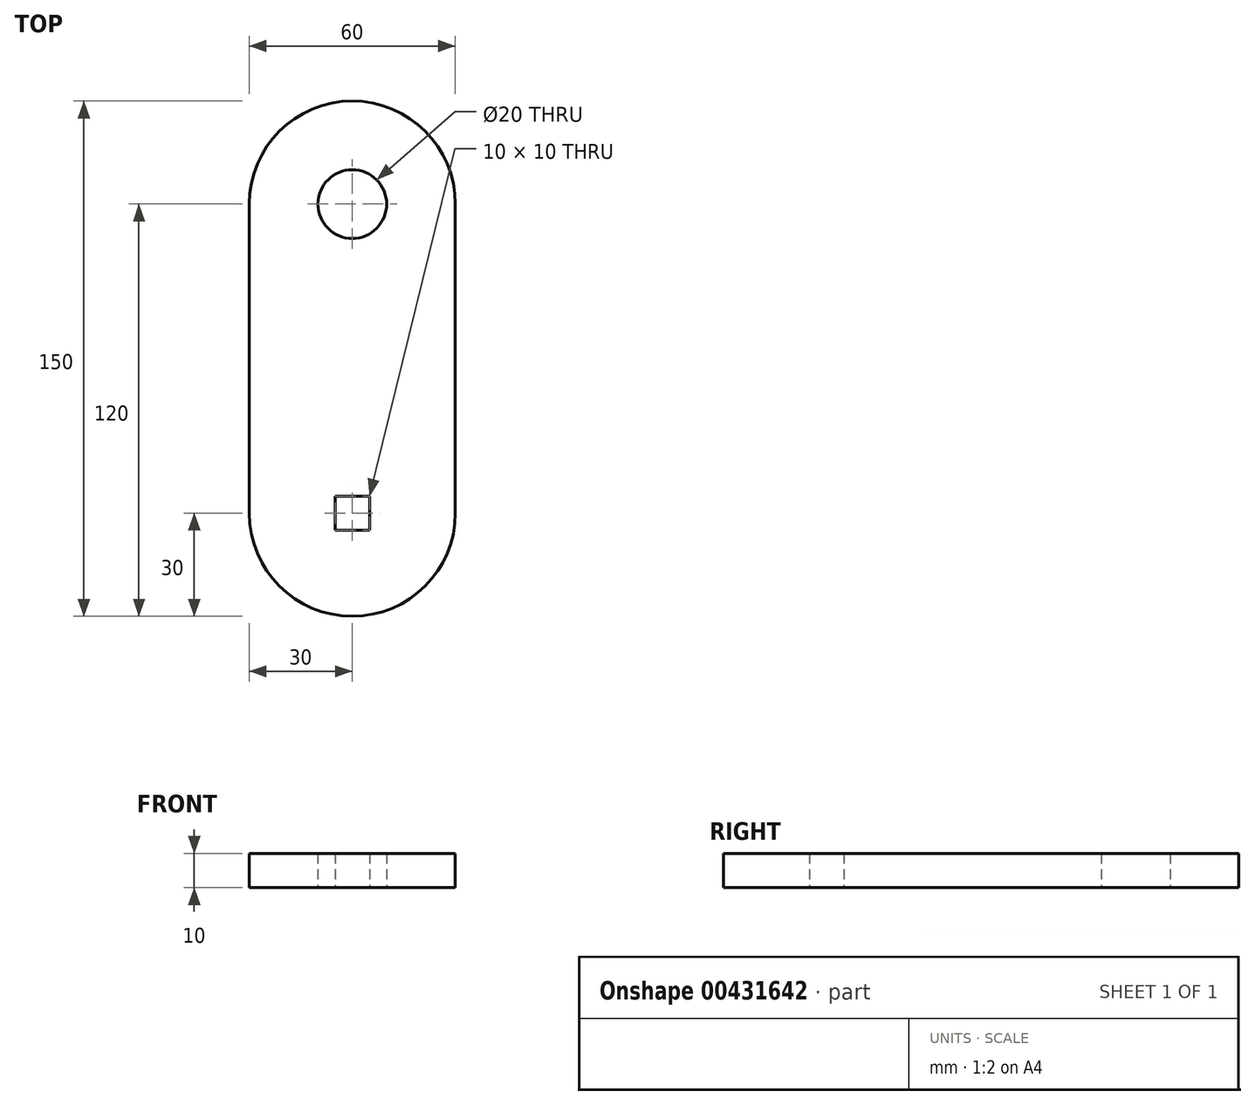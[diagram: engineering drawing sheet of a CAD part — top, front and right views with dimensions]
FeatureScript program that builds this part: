
annotation { "Feature Type Name" : "Feature", "Feature Type Description" : "" }
export const myFeature = defineFeature(function(context is Context, id is Id, definition is map)
    precondition{}
    {
        {
            var Q0;
            Q0=qCreatedBy(makeId("Top.planeOp"),FACE);
            var sketch = newSketch(context, id + "F0", { "sketchPlane" : qUnion([Q0])});
            skLineSegment(sketch, "E0", {"start": v(0, 0) * mm, "end": v(0, 150) * mm, "construction": true});
            skLineSegment(sketch, "E1", {"start": v(0, 0) * mm, "end": v(0, 30) * mm, "construction": true});
            skLineSegment(sketch, "E2", {"start": v(0, 30) * mm, "end": v(-30, 30) * mm});
            skLineSegment(sketch, "E3", {"start": v(-30, 30) * mm, "end": v(30, 30) * mm, "construction": true});
            skArc(sketch, "E4", {"start": v(-30, 30) * mm, "mid": v(0, 0) * mm, "end": v(30, 30) * mm});
            skArc(sketch, "E5", {"start": v(30, 30) * mm, "mid": v(0, 60) * mm, "end": v(-30, 30) * mm, "construction": true});
            skLineSegment(sketch, "E6", {"start": v(0, 150) * mm, "end": v(0, 120) * mm, "construction": true});
            skLineSegment(sketch, "E7", {"start": v(0, 120) * mm, "end": v(30, 120) * mm, "construction": true});
            skLineSegment(sketch, "E8", {"start": v(30, 120) * mm, "end": v(-30, 120) * mm, "construction": true});
            skArc(sketch, "E9", {"start": v(-30, 120) * mm, "mid": v(0, 90) * mm, "end": v(30, 120) * mm, "construction": true});
            skArc(sketch, "E10", {"start": v(30, 120) * mm, "mid": v(0, 150) * mm, "end": v(-30, 120) * mm});
            skLineSegment(sketch, "E11", {"start": v(-30, 120) * mm, "end": v(-30, 30) * mm});
            skLineSegment(sketch, "E12", {"start": v(30, 120) * mm, "end": v(30, 30) * mm});
            skLineSegment(sketch, "E13", {"start": v(0, 30) * mm, "end": v(-5, 30) * mm, "construction": true});
            skLineSegment(sketch, "E14", {"start": v(-5, 30) * mm, "end": v(-5, 25) * mm, "construction": true});
            skLineSegment(sketch, "E15.bottom", {"start": v(-5, 25) * mm, "end": v(5, 25) * mm});
            skLineSegment(sketch, "E15.top", {"start": v(-5, 35) * mm, "end": v(5, 35) * mm});
            skLineSegment(sketch, "E15.left", {"start": v(-5, 25) * mm, "end": v(-5, 35) * mm});
            skLineSegment(sketch, "E15.right", {"start": v(5, 25) * mm, "end": v(5, 35) * mm});
            skCircle(sketch, "E16", {"center": v(0, 120) * mm, "radius": 10 * mm});
            skSolve(sketch);
        }
        {
            var Q0;
            Q0=makeQuery(id+"F0.imprint","IMPRINT",FACE,{"disambiguationData":[TD([[makeQuery(id+"F0.imprint","IMPRINT",EDGE,{"derivedFrom":sQuery(id+"F0.wireOp",EDGE,"E4")}),1.0]])]});
            extrude(context, id + "F1", {"entities" : qUnion([Q0]), "depth" : 10 * mm});
        }
    });
